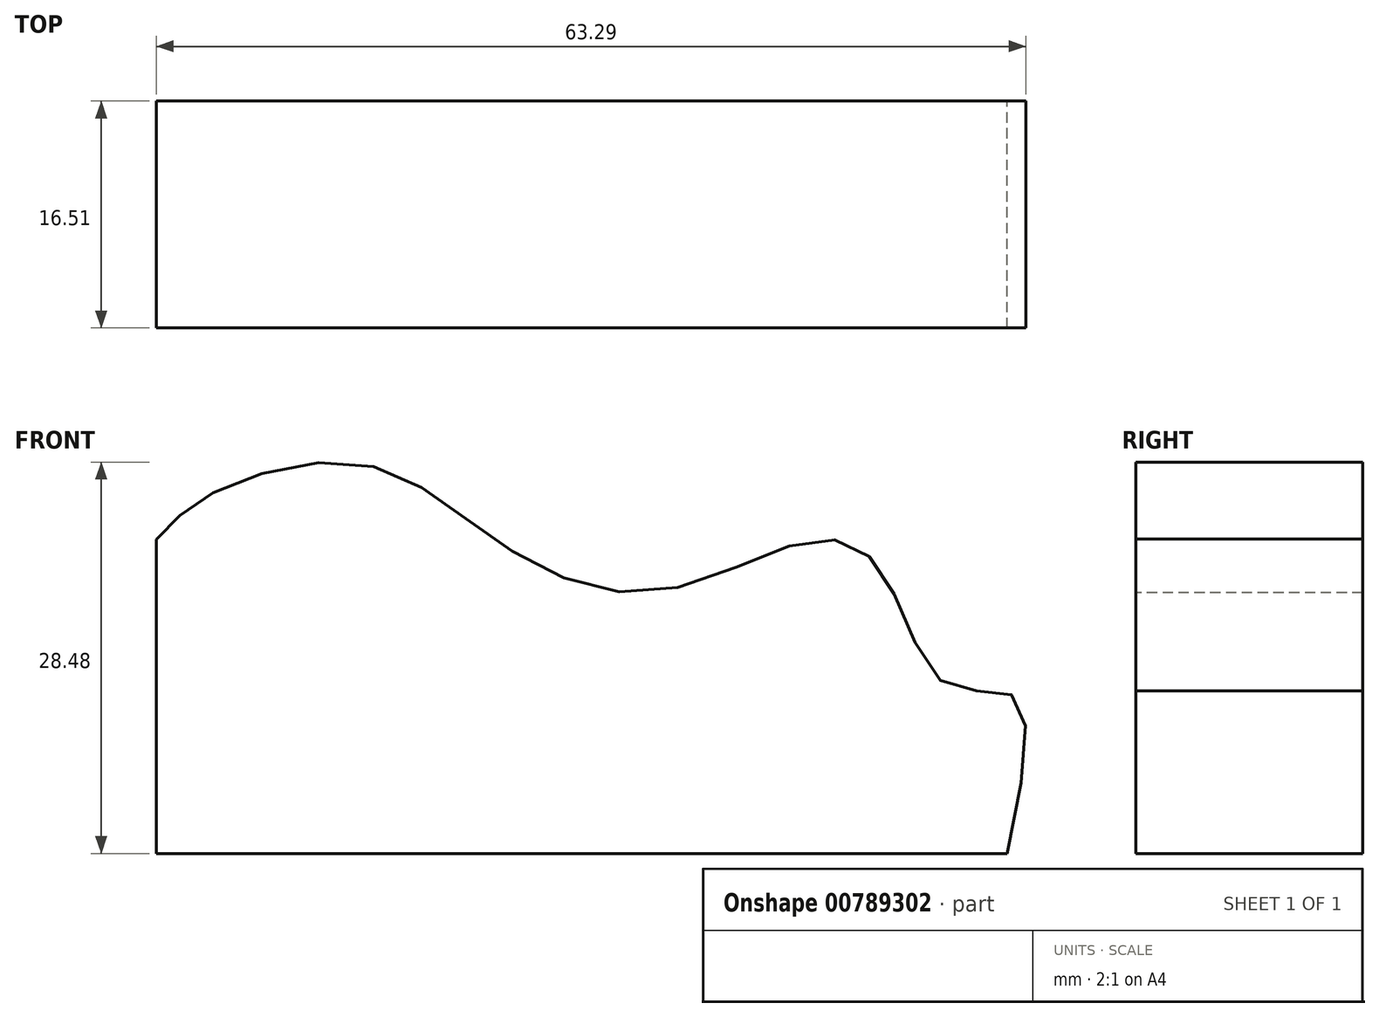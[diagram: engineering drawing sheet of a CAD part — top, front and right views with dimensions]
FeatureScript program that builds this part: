
annotation { "Feature Type Name" : "Feature", "Feature Type Description" : "" }
export const myFeature = defineFeature(function(context is Context, id is Id, definition is map)
    precondition{}
    {
        {
            var Q0;
            Q0=qCreatedBy(makeId("Front.planeOp"),FACE);
            var sketch = newSketch(context, id + "F0", { "sketchPlane" : qUnion([Q0])});
            skLineSegment(sketch, "E0", {"start": v(0, 0) * mm, "end": v(0, 23) * mm});
            skLineSegment(sketch, "E1", {"start": v(-0.4, 0.14) * mm, "end": v(61.91, 0.14) * mm});
            skFitSpline(sketch, "E2", {"points": [v(0, 23) * mm, v(3.95, 26.26) * mm, v(15.1, 28.44) * mm, v(24.63, 23) * mm, v(36.33, 19.19) * mm, v(48.3, 23) * mm, v(53.2, 20) * mm, v(57.56, 12.38) * mm, v(62.46, 11.57) * mm, v(61.91, 0.14) * mm], "startDerivative": vector(36.96, 40.05) * mm, "endDerivative": vector(-26.07, -121.62) * mm});
            skSolve(sketch);
        }
        {
            var Q0;
            {var subQ0=sQuery(id+"F0.wireOp",EDGE,"E2");Q0=makeQuery(id+"F0.imprint","IMPRINT",FACE,{"disambiguationData":[TD([[makeQuery(id+"F0.imprint","IMPRINT",EDGE,{"derivedFrom":subQ0}),-1.0]])]});}
            extrude(context, id + "F1", {"entities" : qUnion([Q0]), "depth" : 16.5 * mm, "offsetDistance" : 25.4 * mm});
        }
    });
